# Revit family: 2056212 Feilo Sylvania Lighting Fixture MYD ADJ WHT 4K PHDIM WHT BEZ
name_source: partatom
category: Lighting Fixtures
revit_build: Autodesk Revit 2017 (Build: 20190507_1515(x64)
units: mm (PartAtom-declared; Revit-internal decimal feet)

## family parameters
Cut with Voids When Loaded = Yes
Host = Face
Light Source = No
OmniClass Number = 23.80.70.00
OmniClass Title = Lighting
Part Type = Normal
Room Calculation Point = No
Round Connector Dimension = Use Diameter
Shared = No

## types (1)
- 2056212 Feilo Sylvania Lighting Fixture MYD ADJ WHT 4K PHDIM WHT BEZ
    AccessoryMaterial = Body-Sylvania-MyriadAdjustableRound-White
    Apparent Load = 10 VA
    Assembly Code = D5020200
    AssetType = Fixed
    BodyMaterial = Body-Sylvania-MyriadAdjustableRound-White
    ClassificationName = Uniclass2015
    ClassificationValue = EF_70_80
    Cost = 0 $
    Default Elevation = 1219 mm
    DiffuserMaterial = Default
    DimmingControlOptions = Non dimmable
    DocumentationLiterature = http://www.sylvania-lighting.com
    DurationUnit = hours
    ElectricShockClassification = Class II
    ExpectedLife = 50000
    IfcExportAs = IfcLightFixtureType
    IfcExportType = IfcLightFixtureType
    ImpactProtectionIndex = IK02
    IngressProtection = IP65
    InputNominalFrequency = 50/60 Hz
    InputVoltage = 230-240V~
    Keynote = 16500
    Lamp = LED
    LampColourRenderingIndex = 0
    LampColourTemperature = 3000 K
    LampNominalLuminous = 1165 lm
    LampType_FEILO = MyriadAdjustableRoundLamp : 2056212 MYD ADJ WHT 4K PHDIM WHT BEZ
    LampsType = LED
    LightOutputRatio = 100
    LuminousEfficacy = 117 lm/W
    Manufacturer = Feilo Sylvania
    ManufacturerName = Feilo Sylvania
    Material = aluminium housing
    Model = MYRIDSQ IP65 FLD 3K STD
    ModelNumber = 2056380
    ModelReference = MYRIDSQ IP65 FLD 3K STD
    Name = MYRIDSQ IP65 FLD 3K STD
    NominalDepth = 72 mm
    NominalHeight = 64 mm
    NominalLength = 72 mm
    PowerConsumption = 10 W
    PowerFactor = 0
    ReflectorMaterial = Default
    SphereRadius_FEILO = 27 mm
    Type Image = <None>
    TypeName = MYRIDSQ IP65 FLD 3K STD
    URL = http://www.sylvania-lighting.com
    Voltage = 230 V
    Weight = 0.39 kg

## geometry (parser evidence)
native form markers: Sweep x7
no freeform markers — native parametric forms only
